# Revit family: FT ATEX LED MAX_2021
name_source: partatom
category: Luminarias
units: mm (PartAtom-declared; Revit-internal decimal feet)

## family parameters
Compartido = No
Corte con vacíos al cargar = No
Cota de conector redondo = Diámetro de uso
Número OmniClass = 23.80.70.00
Origen de luz = Sí
Punto de cálculo de habitación = No
Se basa en plano de trabajo = No
Siempre vertical = Sí
Tipo de pieza = Normal
Título OmniClass = Lighting

## types (12) — shared parameters
Anchura rectángulo de emisión = 610 mm
Cambio de temperatura de color de luz atenuada = <Ninguno>
Descripción = https://www.airfal.com
EX Area = II 3GD Ex nR IIC T5 Gc Ex tb IIIC 100ºC Dc
Emergency system = No
Filtro de color = 16777215
Forma visible en renderización = No
IK = IK07
IP = IP66
Led Module = Sí
Longitud de rectángulo de emisión = 1219 mm
URL = https://www.airfal.com
Ángulo de inclinación = 90.00°
zero-valued in all types: Elevación por defecto

## per-type parameters (varying)
| type | Archivo de red fotométrica | Equiv MH | Modules | Position | Power |
| PA104A | PA104A.ies | 70 W | 2 | 90.00° | 48 W |
| PA204A | PA204A.ies | 150 W | 4 | 90.00° | 97 W |
| PA304A | PA304A.ies | 250 W | 6 | 90.00° | 146 W |
| PA404A | PA404A.ies | 400 W | 8 | 50.00° | 194 W |
| PA404B | PA404B.ies | 400 W | 8 | 50.00° | 194 W |
| PA404C | PA404C.ies | 400 W | 8 | 50.00° | 194 W |
| PA104B | PA104B.ies | 70 W | 2 | 60.00° | 48 W |
| PA104C | PA104C.ies | 70 W | 2 | 90.00° | 48 W |
| PA204B | PA204B.ies | 150 W | 4 | 90.00° | 97 W |
| PA204C | PA204C.ies | 150 W | 4 | 90.00° | 97 W |
| PA304B | PA304B.ies | 250 W | 6 | 90.00° | 146 W |
| PA304C | PA304C.ies | 250 W | 6 | 90.00° | 146 W |

## geometry (parser evidence)
native form markers: Blend x8, Sweep x15
no freeform markers — native parametric forms only
